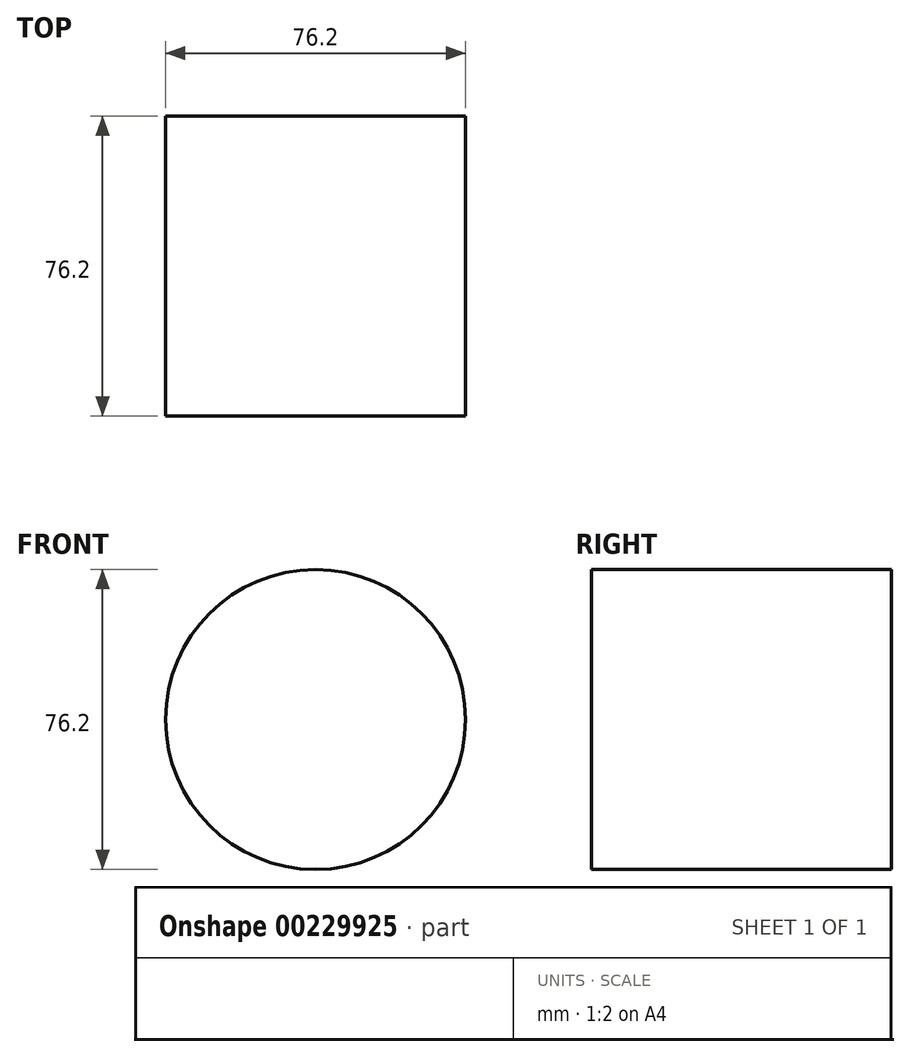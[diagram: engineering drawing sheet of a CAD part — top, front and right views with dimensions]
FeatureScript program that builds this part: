
annotation { "Feature Type Name" : "Feature", "Feature Type Description" : "" }
export const myFeature = defineFeature(function(context is Context, id is Id, definition is map)
    precondition{}
    {
        {
            var Q0;
            Q0=qCreatedBy(makeId("Front.planeOp"),FACE);
            var sketch = newSketch(context, id + "F1", { "sketchPlane" : qUnion([Q0])});
            skCircle(sketch, "E0", {"center": v(0, 0) * mm, "radius": 38.1 * mm});
            skSolve(sketch);
        }
        {
            var Q0;
            Q0=makeQuery(id+"F1.imprint","IMPRINT",FACE,{"disambiguationData":[TD([[makeQuery(id+"F1.imprint","IMPRINT",EDGE,{"derivedFrom":sQuery(id+"F1.wireOp",EDGE,"E0")}),1.0]])]});
            extrude(context, id + "F0", {"entities" : qUnion([Q0]), "depth" : 76.2 * mm});
        }
    });
